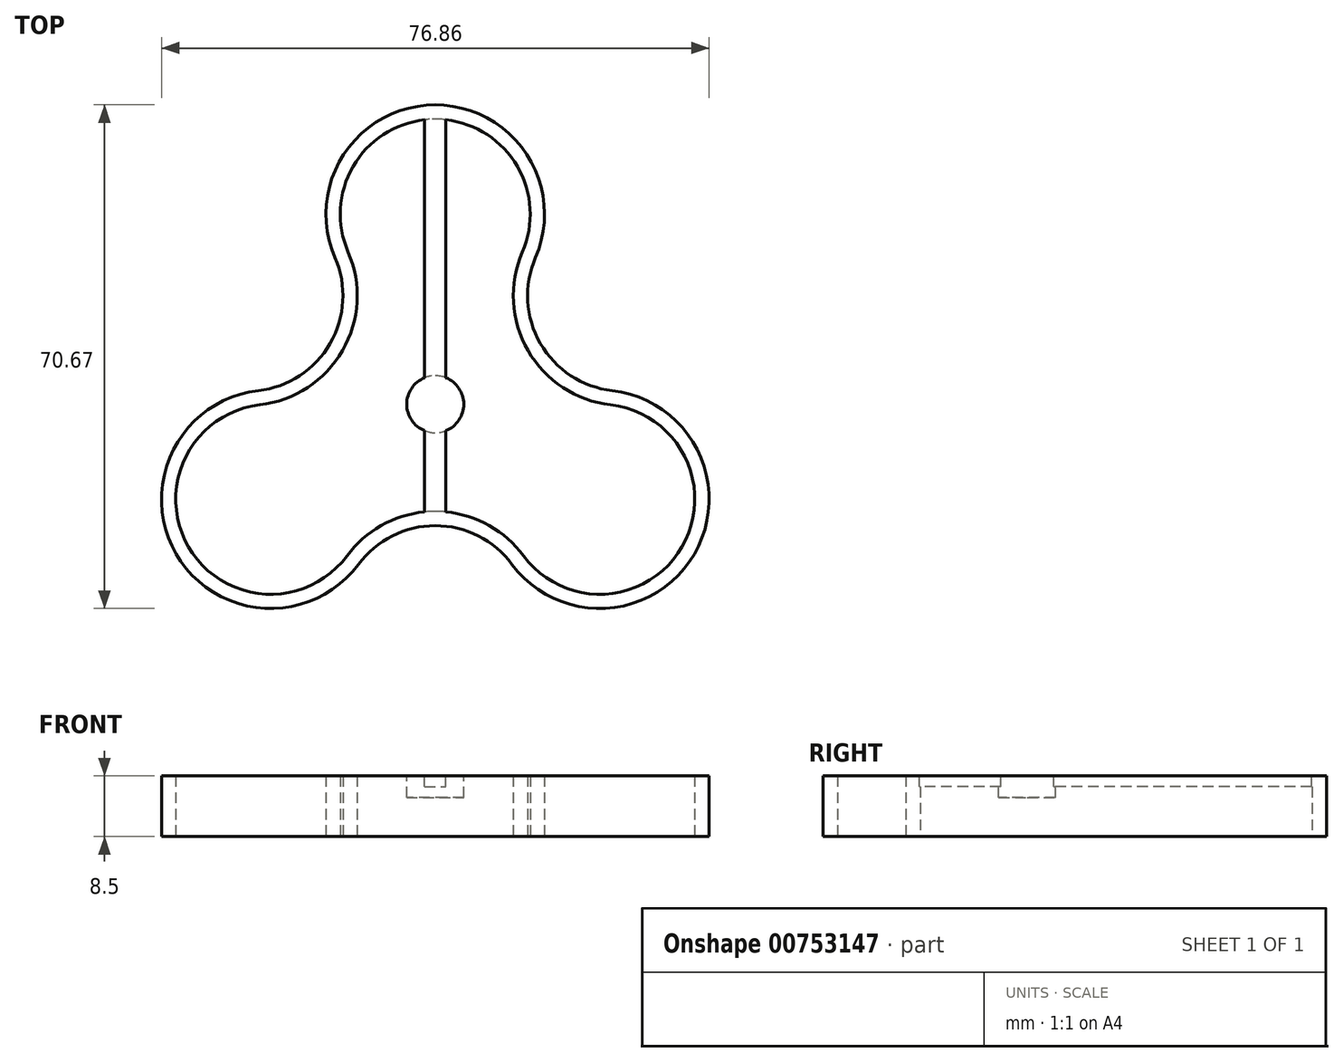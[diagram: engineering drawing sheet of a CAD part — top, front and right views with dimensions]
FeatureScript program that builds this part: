
annotation { "Feature Type Name" : "Feature", "Feature Type Description" : "" }
export const myFeature = defineFeature(function(context is Context, id is Id, definition is map)
    precondition{}
    {
        {
            var Q0;
            Q0=qCreatedBy(makeId("Top.planeOp"),FACE);
            var sketch = newSketch(context, id + "F0", { "sketchPlane" : qUnion([Q0])});
            skArc(sketch, "E0", {"start": v(12.23, 21.36) * mm, "mid": v(0, 40) * mm, "end": v(-12.23, 21.36) * mm});
            skArc(sketch, "E1", {"start": v(-24.61, -0.09) * mm, "mid": v(-34.64, -20) * mm, "end": v(-12.38, -21.27) * mm});
            skArc(sketch, "E2", {"start": v(12.38, -21.27) * mm, "mid": v(34.64, -20) * mm, "end": v(24.61, -0.09) * mm});
            skArc(sketch, "E3", {"start": v(-24.61, -0.09) * mm, "mid": v(-13.02, 7.52) * mm, "end": v(-12.23, 21.36) * mm});
            skArc(sketch, "E4", {"start": v(12.23, 21.36) * mm, "mid": v(13.02, 7.52) * mm, "end": v(24.61, -0.09) * mm});
            skArc(sketch, "E5", {"start": v(12.38, -21.27) * mm, "mid": v(0, -15.04) * mm, "end": v(-12.38, -21.27) * mm});
            skLineSegment(sketch, "E6", {"start": v(0, 0) * mm, "end": v(26.37, 15.23) * mm, "construction": true});
            skLineSegment(sketch, "E7", {"start": v(0, 0) * mm, "end": v(-26.37, 15.23) * mm, "construction": true});
            skLineSegment(sketch, "E8", {"start": v(0, 0) * mm, "end": v(0, -30.45) * mm, "construction": true});
            skLineSegment(sketch, "E9", {"start": v(0, 0) * mm, "end": v(0, 26.67) * mm, "construction": true});
            skLineSegment(sketch, "E10", {"start": v(0, 0) * mm, "end": v(-23.1, -13.33) * mm, "construction": true});
            skLineSegment(sketch, "E11", {"start": v(0, 0) * mm, "end": v(23.1, -13.33) * mm, "construction": true});
            skArc(sketch, "E12.0", {"start": v(14.07, 20.56) * mm, "mid": v(14.76, 8.52) * mm, "end": v(24.84, 1.9) * mm});
            skArc(sketch, "E12.1", {"start": v(-24.84, 1.9) * mm, "mid": v(-14.76, 8.52) * mm, "end": v(-14.07, 20.56) * mm});
            skArc(sketch, "E12.2", {"start": v(-24.84, 1.9) * mm, "mid": v(-36.37, -21) * mm, "end": v(-10.78, -22.46) * mm});
            skArc(sketch, "E12.3", {"start": v(14.07, 20.56) * mm, "mid": v(0, 42) * mm, "end": v(-14.07, 20.56) * mm});
            skArc(sketch, "E12.4", {"start": v(10.78, -22.46) * mm, "mid": v(0, -17.04) * mm, "end": v(-10.78, -22.46) * mm});
            skArc(sketch, "E12.5", {"start": v(10.78, -22.46) * mm, "mid": v(36.37, -21) * mm, "end": v(24.84, 1.9) * mm});
            skSolve(sketch);
        }
        {
            var Q0;
            Q0=qSketchRegion(id+"F0",true);
            extrude(context, id + "F1", {"entities" : qUnion([Q0]), "depth" : 8.5 * mm, "offsetDistance" : 25 * mm});
        }
        {
            var Q0;
            Q0=makeQuery(id+"F1.opExtrude","CAP_FACE",FACE,{"disambiguationData":[OSD([sQuery(id+"F0.wireOp",EDGE,"E0"),sQuery(id+"F0.wireOp",EDGE,"E1"),sQuery(id+"F0.wireOp",EDGE,"E2"),sQuery(id+"F0.wireOp",EDGE,"E3"),sQuery(id+"F0.wireOp",EDGE,"E4"),sQuery(id+"F0.wireOp",EDGE,"E5"),sQuery(id+"F0.wireOp",EDGE,"E12.0"),sQuery(id+"F0.wireOp",EDGE,"E12.1"),sQuery(id+"F0.wireOp",EDGE,"E12.2"),sQuery(id+"F0.wireOp",EDGE,"E12.3"),sQuery(id+"F0.wireOp",EDGE,"E12.4"),sQuery(id+"F0.wireOp",EDGE,"E12.5")])],"isStart":false});
            var sketch = newSketch(context, id + "F2", { "sketchPlane" : qUnion([Q0])});
            skLineSegment(sketch, "E13", {"start": v(-1.5, 39.92) * mm, "end": v(-1.5, -15.11) * mm});
            skLineSegment(sketch, "E14", {"start": v(1.5, -15.11) * mm, "end": v(1.5, 39.92) * mm});
            skArc(sketch, "E15", {"start": v(1.5, 39.92) * mm, "mid": v(0, 40) * mm, "end": v(-1.5, 39.92) * mm});
            skArc(sketch, "E16", {"start": v(1.5, -15.11) * mm, "mid": v(0, -15.04) * mm, "end": v(-1.5, -15.11) * mm});
            skSolve(sketch);
        }
        {
            var Q0;
            Q0 = qSketchRegion(id + "F2", true);
            extrude(context, id + "F3", {"entities" : qUnion([Q0]), "operationType" : NewBodyOperationType.ADD, "oppositeDirection" : true, "depth" : 1.5 * mm, "offsetDistance" : 25 * mm});
        }
        {
            var Q0;
            Q0=makeQuery(id+"F3.opExtrude","CAP_FACE",FACE,{"disambiguationData":[OSD([sQuery(id+"F2.wireOp",EDGE,"E13"),sQuery(id+"F2.wireOp",EDGE,"E14"),sQuery(id+"F2.wireOp",EDGE,"E15"),sQuery(id+"F2.wireOp",EDGE,"E16")])],"isStart":false});
            var sketch = newSketch(context, id + "F4", { "sketchPlane" : qUnion([Q0])});
            skCircle(sketch, "E17", {"center": v(0, 0) * mm, "radius": 4 * mm});
            skSolve(sketch);
        }
        {
            var Q0;
            Q0 = qSketchRegion(id + "F4", true);
            extrude(context, id + "F5", {"entities" : qUnion([Q0]), "operationType" : NewBodyOperationType.ADD, "endBound" : BoundingType.SYMMETRIC, "depth" : 3 * mm, "offsetDistance" : 25 * mm});
        }
    });
